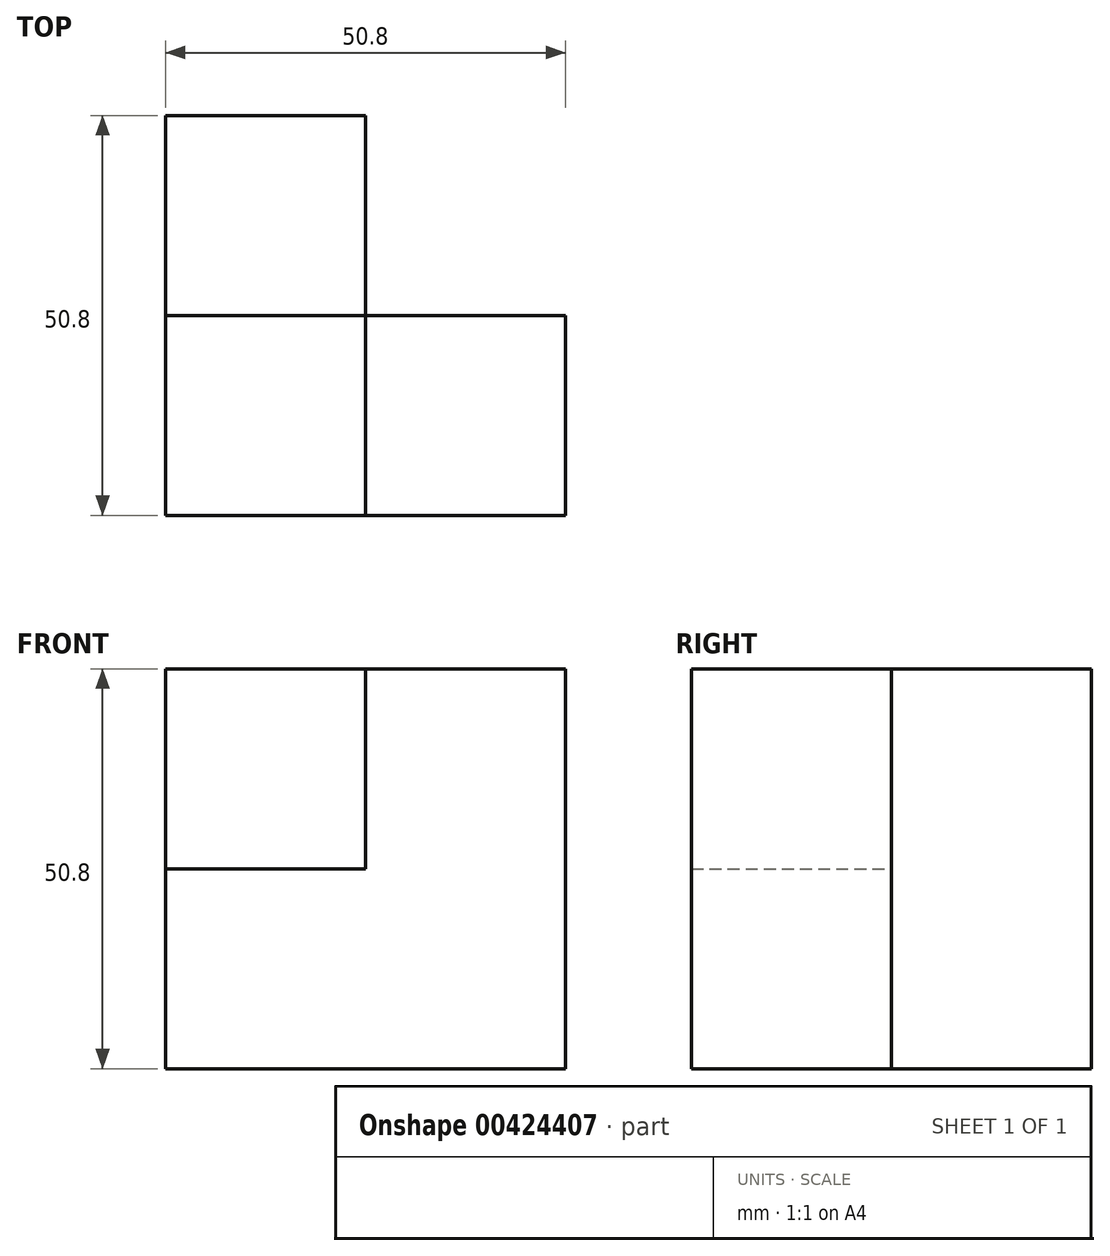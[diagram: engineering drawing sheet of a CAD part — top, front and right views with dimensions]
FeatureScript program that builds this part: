
annotation { "Feature Type Name" : "Feature", "Feature Type Description" : "" }
export const myFeature = defineFeature(function(context is Context, id is Id, definition is map)
    precondition{}
    {
        {
            var Q0;
            Q0=qCreatedBy(makeId("Front.planeOp"),FACE);
            var sketch = newSketch(context, id + "F0", { "sketchPlane" : qUnion([Q0])});
            skLineSegment(sketch, "E0.bottom", {"start": v(0, 0) * mm, "end": v(25.4, 0) * mm});
            skLineSegment(sketch, "E0.top", {"start": v(0, 25.4) * mm, "end": v(25.4, 25.4) * mm});
            skLineSegment(sketch, "E0.left", {"start": v(0, 0) * mm, "end": v(0, 25.4) * mm});
            skLineSegment(sketch, "E0.right", {"start": v(25.4, 0) * mm, "end": v(25.4, 25.4) * mm});
            skLineSegment(sketch, "E1.bottom", {"start": v(25.4, 25.4) * mm, "end": v(50.8, 25.4) * mm});
            skLineSegment(sketch, "E1.top", {"start": v(25.4, 0) * mm, "end": v(50.8, 0) * mm});
            skLineSegment(sketch, "E1.left", {"start": v(25.4, 25.4) * mm, "end": v(25.4, 0) * mm});
            skLineSegment(sketch, "E1.right", {"start": v(50.8, 25.4) * mm, "end": v(50.8, 0) * mm});
            skLineSegment(sketch, "E2.top", {"start": v(25.4, 50.8) * mm, "end": v(50.8, 50.8) * mm});
            skLineSegment(sketch, "E2.left", {"start": v(25.4, 25.4) * mm, "end": v(25.4, 50.8) * mm});
            skLineSegment(sketch, "E2.right", {"start": v(50.8, 25.4) * mm, "end": v(50.8, 50.8) * mm});
            skSolve(sketch);
        }
        {
            var Q0;
            Q0=makeQuery(id+"F0.imprint","IMPRINT",FACE,{"disambiguationData":[TD([[makeQuery(id+"F0.imprint","IMPRINT",EDGE,{"derivedFrom":sQuery(id+"F0.wireOp",EDGE,"E0.bottom")}),1.0]])]});
            var Q1;
            Q1=makeQuery(id+"F0.imprint","IMPRINT",FACE,{"disambiguationData":[TD([[makeQuery(id+"F0.imprint","IMPRINT",EDGE,{"derivedFrom":sQuery(id+"F0.wireOp",EDGE,"E1.top")}),1.0]])]});
            var Q2;
            Q2=makeQuery(id+"F0.imprint","IMPRINT",FACE,{"disambiguationData":[TD([[makeQuery(id+"F0.imprint","IMPRINT",EDGE,{"derivedFrom":sQuery(id+"F0.wireOp",EDGE,"E1.bottom")}),1.0]])]});
            extrude(context, id + "F1", {"entities" : qUnion([Q0, Q1, Q2]), "depth" : 25.4 * mm});
        }
        {
            var Q0;
            Q0=makeQuery(id+"F1.opExtrude","CAP_FACE",FACE,{"disambiguationData":[OSD([sQuery(id+"F0.wireOp",EDGE,"E0.bottom"),sQuery(id+"F0.wireOp",EDGE,"E0.top"),sQuery(id+"F0.wireOp",EDGE,"E0.left"),sQuery(id+"F0.wireOp",EDGE,"E1.top"),sQuery(id+"F0.wireOp",EDGE,"E1.right"),sQuery(id+"F0.wireOp",EDGE,"E2.top"),sQuery(id+"F0.wireOp",EDGE,"E2.left"),sQuery(id+"F0.wireOp",EDGE,"E2.right")])],"isStart":true});
            var sketch = newSketch(context, id + "F2", { "sketchPlane" : qUnion([Q0])});
            skLineSegment(sketch, "E3.bottom", {"start": v(-25.4, 25.4) * mm, "end": v(0, 25.4) * mm});
            skLineSegment(sketch, "E3.top", {"start": v(-25.4, 0) * mm, "end": v(0, 0) * mm});
            skLineSegment(sketch, "E3.left", {"start": v(-25.4, 25.4) * mm, "end": v(-25.4, 0) * mm});
            skLineSegment(sketch, "E3.right", {"start": v(0, 25.4) * mm, "end": v(0, 0) * mm});
            skLineSegment(sketch, "E4.top", {"start": v(-25.4, 50.8) * mm, "end": v(0, 50.8) * mm});
            skLineSegment(sketch, "E4.left", {"start": v(-25.4, 25.4) * mm, "end": v(-25.4, 50.8) * mm});
            skLineSegment(sketch, "E4.right", {"start": v(0, 25.4) * mm, "end": v(0, 50.8) * mm});
            skSolve(sketch);
        }
        {
            var Q0;
            Q0=makeQuery(id+"F2.imprint","IMPRINT",FACE,{"disambiguationData":[TD([[makeQuery(id+"F2.imprint","IMPRINT",EDGE,{"derivedFrom":sQuery(id+"F2.wireOp",EDGE,"E3.bottom")}),-1.0]])]});
            var Q1;
            Q1=makeQuery(id+"F2.imprint","IMPRINT",FACE,{"disambiguationData":[TD([[makeQuery(id+"F2.imprint","IMPRINT",EDGE,{"derivedFrom":sQuery(id+"F2.wireOp",EDGE,"E3.top")}),-1.0]])]});
            extrude(context, id + "F3", {"entities" : qUnion([Q0, Q1]), "depth" : 25.4 * mm});
        }
    });
